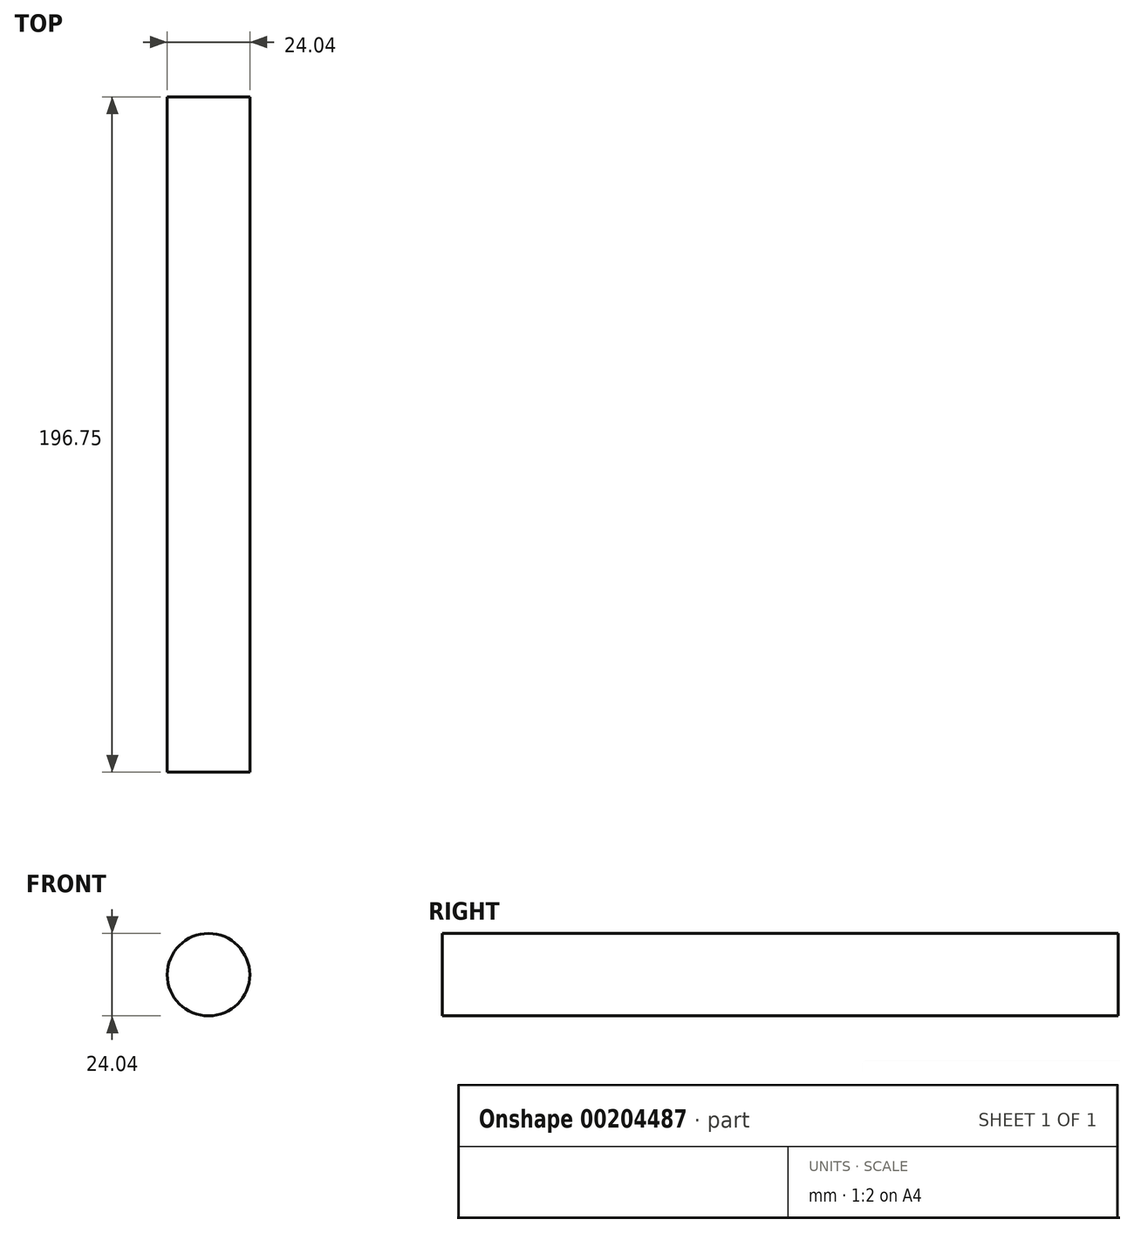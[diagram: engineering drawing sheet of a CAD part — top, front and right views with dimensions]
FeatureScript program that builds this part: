
annotation { "Feature Type Name" : "Feature", "Feature Type Description" : "" }
export const myFeature = defineFeature(function(context is Context, id is Id, definition is map)
    precondition{}
    {
        {
            var Q0;
            Q0=qCreatedBy(makeId("Front.planeOp"),FACE);
            var sketch = newSketch(context, id + "F0", { "sketchPlane" : qUnion([Q0])});
            skCircle(sketch, "E0", {"center": v(0, 0) * mm, "radius": 12.02 * mm});
            skSolve(sketch);
        }
        {
            var Q0;
            Q0=makeQuery(id+"F0.imprint","IMPRINT",FACE,{"disambiguationData":[TD([[makeQuery(id+"F0.imprint","IMPRINT",EDGE,{"derivedFrom":sQuery(id+"F0.wireOp",EDGE,"E0")}),1.0]])]});
            extrude(context, id + "F1", {"entities" : qUnion([Q0]), "depth" : 105.33 * mm});
        }
        {
            var Q0;
            Q0=makeQuery(id+"F1.opExtrude","CAP_FACE",FACE,{"disambiguationData":[OSD([sQuery(id+"F0.wireOp",EDGE,"E0")])],"isStart":true});
            extrude(context, id + "F2", {"entities" : qUnion([Q0]), "operationType" : NewBodyOperationType.ADD, "depth" : 91.42 * mm});
        }
    });
